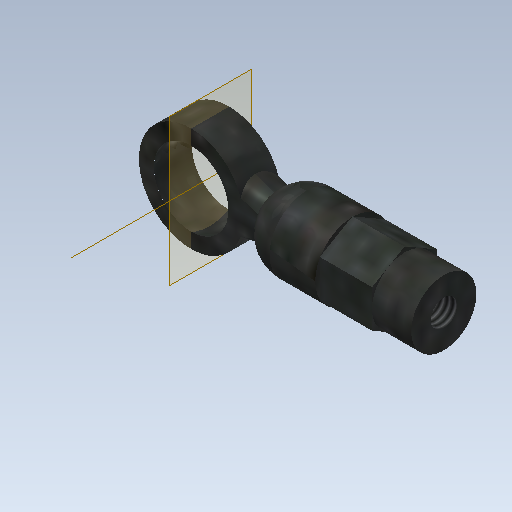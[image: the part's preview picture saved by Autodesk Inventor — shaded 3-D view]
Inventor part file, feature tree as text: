
AUTODESK INVENTOR PART (.ipt)
format: ipt  version: 2020 (Build 240168000, 168)  size: 272,896 bytes
history: native  units: mm
features: sketch x11, extrude x6, revolve x4, projected_geometry x4, hole x2, plane x1, other x1
ambient origin geometry x8: Origin, YZ Plane, XZ Plane, XY Plane, X Axis, Y Axis, Z Axis, Center Point
bodies: Solid1 (feature_tree)
feature tree (29):
  revolve  "Revolution1"  [1 undecoded]
  extrude  "Extrusion1"  Depth=10.2mm
  plane  "Work Plane1"
  revolve  "Revolution2"  [1 undecoded]
  hole  "Hole2"  [1 undecoded]
  extrude  "Extrusion2"  TaperAngle=0.0deg  [1 undecoded]
  extrude  "Extrusion3"  TaperAngle=90.0deg  [1 undecoded]
  hole  "Hole3"  [1 undecoded]
  extrude  "Extrusion4"  Depth=5.0mm
  extrude  "Extrusion5"  Depth=10.0mm
  revolve  "Revolution3"  [1 undecoded]
  revolve  "Revolution4"  [1 undecoded]
  extrude  "Extrusion6"  TaperAngle=90.0deg  [1 undecoded]
  sketch  "Sketch1"  dims[d0=2.85mm d1=3.5mm]
  sketch  "Sketch2"  dims[d2=90.0deg d3=10.2mm]
  other  "Work Axis1"
  sketch  "Sketch3"  dims[d4=10.9mm d7=8.0mm]
  sketch  "Sketch4"  dims[d10=2.9mm d11=0.0mm d12=19.198622mm]
  sketch  "Sketch5"  dims[d13=19.198622mm d25=0.0mm]
  sketch  "Sketch6"  dims[d26=6.4mm d27=90.0deg]
  sketch  "Sketch9"  dims[d28=1.0mm d29=1.0mm d30=4.0mm d31=2.0mm d32=90.0deg d33=0.5mm d34=20.594885mm d35=5.0mm]
  sketch  "Sketch10"  dims[d36=4.0mm d37=0.0mm d38=5.0mm]
  sketch  "Sketch11"  dims[d39=3.0mm d40=0.0mm d41=10.0mm d42=10.0mm]
  sketch  "Sketch12"  dims[d43=2.013mm d44=4.0mm d45=4.0mm d46=2.0mm d47=90.0deg d48=5.7mm d49=20.594885mm d50=8.0mm]
  sketch  "Sketch13"  dims[d51=0.0mm d52=0.0mm d53=10.0mm d54=0.0mm d55=90.0deg d56=90.0deg d57=10.0mm d58=0.0mm]
  projected_geometry  "Projected Loop1"
  projected_geometry  "Project Cut Edges1"
  projected_geometry  "Project Cut Edges2"
  projected_geometry  "Project Cut Edges3"
note: 9 required parameter values undecoded (feature->parameter linkage not recoverable at this tier; creation-order binding heuristic only, values carry confidence <= 0.55)